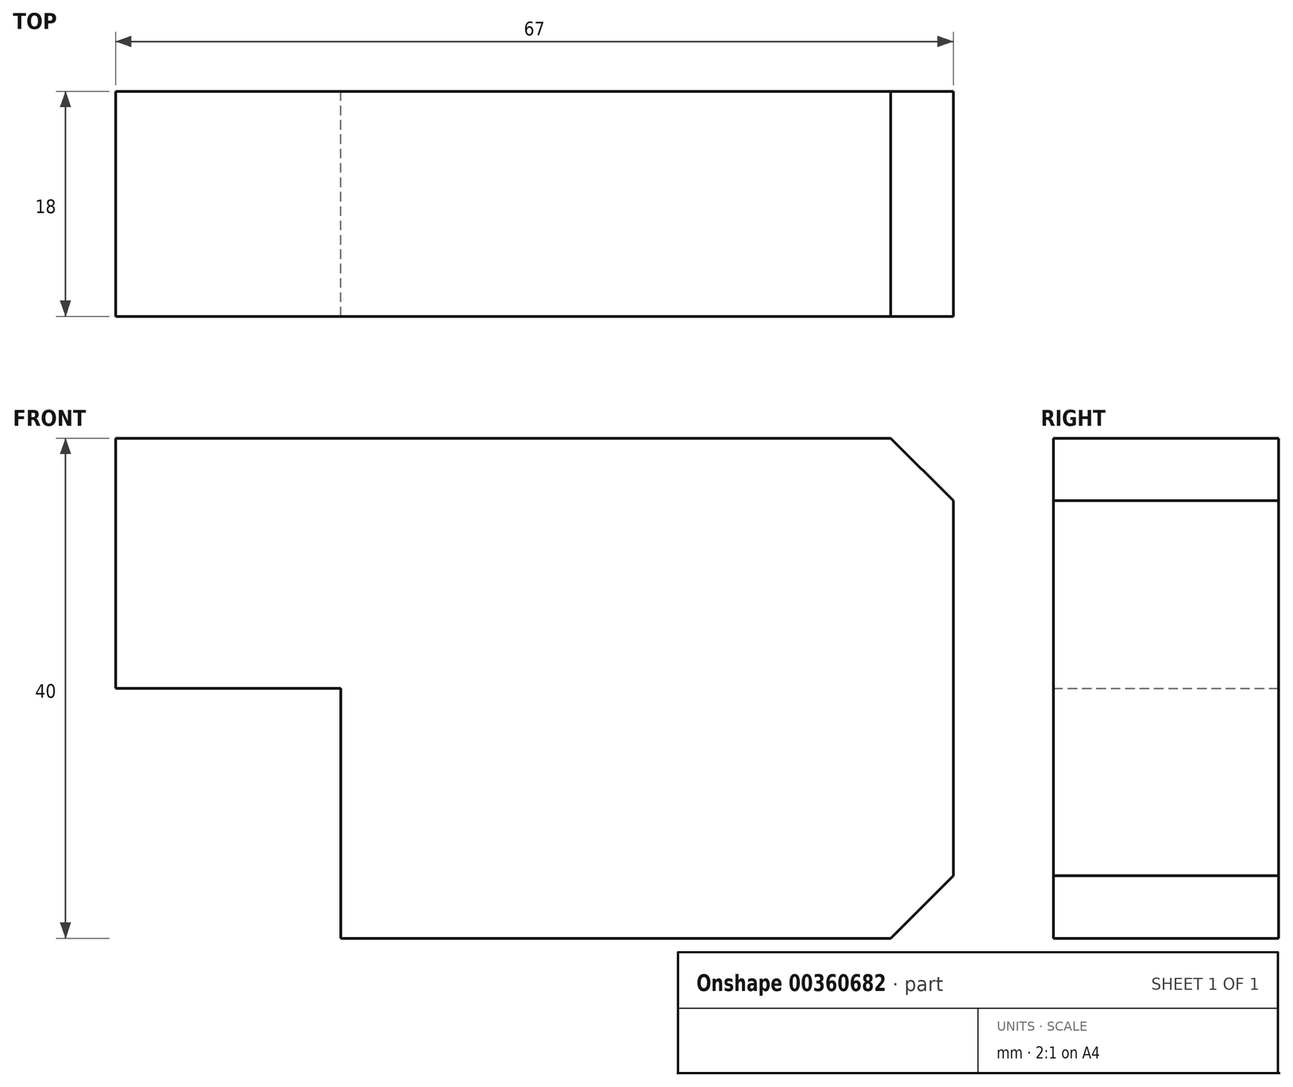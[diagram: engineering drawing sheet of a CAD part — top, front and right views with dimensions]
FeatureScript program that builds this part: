
annotation { "Feature Type Name" : "Feature", "Feature Type Description" : "" }
export const myFeature = defineFeature(function(context is Context, id is Id, definition is map)
    precondition{}
    {
        {
            var Q0;
            Q0=qCreatedBy(makeId("Front.planeOp"),FACE);
            var sketch = newSketch(context, id + "F0", { "sketchPlane" : qUnion([Q0])});
            skLineSegment(sketch, "E0.bottom", {"start": v(18, 0) * mm, "end": v(67, 0) * mm});
            skLineSegment(sketch, "E0.top", {"start": v(0, 40) * mm, "end": v(67, 40) * mm});
            skLineSegment(sketch, "E0.left", {"start": v(0, 20) * mm, "end": v(0, 40) * mm});
            skLineSegment(sketch, "E0.right", {"start": v(67, 0) * mm, "end": v(67, 40) * mm});
            skLineSegment(sketch, "E1.top", {"start": v(0, 20) * mm, "end": v(18, 20) * mm});
            skLineSegment(sketch, "E1.right", {"start": v(18, 0) * mm, "end": v(18, 20) * mm});
            skPoint(sketch, "E2.orphan", {"position": v(0, 0) * mm});
            skSolve(sketch);
        }
        {
            var Q0;
            Q0=makeQuery(id+"F0.imprint","IMPRINT",FACE,{"disambiguationData":[TD([[makeQuery(id+"F0.imprint","IMPRINT",EDGE,{"derivedFrom":sQuery(id+"F0.wireOp",EDGE,"E0.bottom")}),1.0]])]});
            extrude(context, id + "F1", {"entities" : qUnion([Q0]), "depth" : 18 * mm});
        }
        {
            var Q0;
            Q0=makeQuery(id+"F1.opExtrude","SWEPT_EDGE",EDGE,{"disambiguationData":[OSD([sQuery(id+"F0.wireOp",EDGE,"E0.top"),sQuery(id+"F0.wireOp",EDGE,"E0.right")])]});
            var Q1;
            Q1=makeQuery(id+"F1.opExtrude","SWEPT_EDGE",EDGE,{"disambiguationData":[OSD([sQuery(id+"F0.wireOp",EDGE,"E0.bottom"),sQuery(id+"F0.wireOp",EDGE,"E0.right")])]});
            chamfer(context, id + "F2", {"entities" : qUnion([Q0, Q1]), "width" : 5 * mm, "tangentPropagation" : true});
        }
    });
